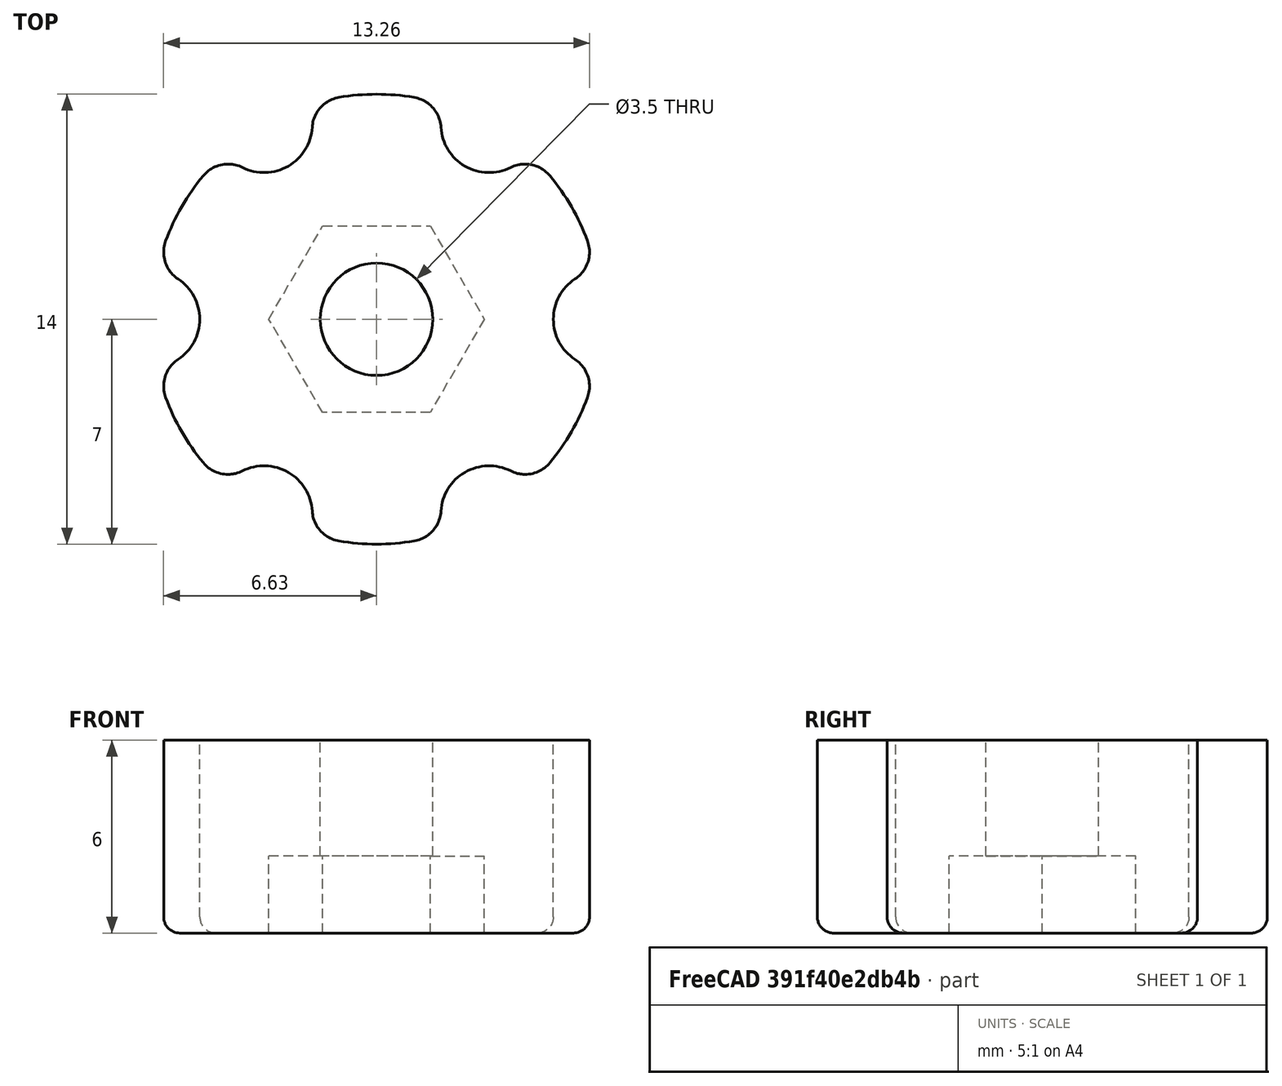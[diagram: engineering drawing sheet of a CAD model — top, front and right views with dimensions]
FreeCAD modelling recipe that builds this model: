
FCSTD DOCUMENT  (FreeCAD 0.19R24267 +99 (Git))
Label: ajustadorM3
License: All rights reserved
LicenseURL: http://en.wikipedia.org/wiki/All_rights_reserved
objects: Part::Cylinder×8, Part::Fillet×7, Part::MultiFuse×2, Part::Prism×1, Part::Cut×1, Part::Refine×1
note: 20 computed .brp shape members not serialized (recipe doc carries the construction recipe); baked Part::Feature solids carry a one-line shape summary decoded from their .brp

FEATURE [Part::Cylinder] cylinder
  Angle = 360
  AttacherType = Attacher::AttachEngine3D
  Height = 6
  Radius = 7
FEATURE [Part::Cylinder] cylinder001
  Angle = 360
  AttacherType = Attacher::AttachEngine3D
  Height = 100
  Placement = pos=(7,0,-50) rot=(0,0,1;0rad)
  Radius = 1.5
FEATURE [Part::Cylinder] cylinder002
  Angle = 360
  AttacherType = Attacher::AttachEngine3D
  Height = 100
  Placement = pos=(3.5,6.06218,-50) rot=(0,0,1;1.0472rad)
  Radius = 1.5
FEATURE [Part::Cylinder] cylinder003
  Angle = 360
  AttacherType = Attacher::AttachEngine3D
  Height = 100
  Placement = pos=(-3.5,6.06218,-50) rot=(0,0,1;2.0944rad)
  Radius = 1.5
FEATURE [Part::Cylinder] cylinder004
  Angle = 360
  AttacherType = Attacher::AttachEngine3D
  Height = 100
  Placement = pos=(-7,9e-16,-50) rot=(0,0,1;3.14159rad)
  Radius = 1.5
FEATURE [Part::Cylinder] cylinder005
  Angle = 360
  AttacherType = Attacher::AttachEngine3D
  Height = 100
  Placement = pos=(-3.5,-6.06218,-50) rot=(0,0,1;4.18879rad)
  Radius = 1.5
FEATURE [Part::Cylinder] cylinder006
  Angle = 360
  AttacherType = Attacher::AttachEngine3D
  Height = 100
  Placement = pos=(3.5,-6.06218,-50) rot=(0,0,-1;1.0472rad)
  Radius = 1.5
FEATURE [Part::MultiFuse] Group
  Shapes = -> [cylinder001,cylinder002,cylinder003,cylinder004,cylinder005,cylinder006]
FEATURE [Part::Prism] prism
  AttacherType = Attacher::AttachEngine3D
  Circumradius = 3.35
  FirstAngle = 0
  Height = 4.8
  Placement = pos=(0,0,-2.4) rot=(0,0,1;0rad)
  Polygon = 6
  SecondAngle = 0
FEATURE [Part::Cylinder] cylinder007
  Angle = 360
  AttacherType = Attacher::AttachEngine3D
  Height = 20
  Placement = pos=(0,0,-10) rot=(0,0,1;0rad)
  Radius = 1.75
FEATURE [Part::MultiFuse] union
  Shapes = -> [Group,prism,cylinder007]
FEATURE [Part::Cut] difference
  Base = -> cylinder
  Tool = -> union
FEATURE [Part::Refine] difference001
  Source = -> difference
FEATURE [Part::Fillet] Fillet
  Base = -> difference001
  Edges = 1 edges r=1: [Edge25]
FEATURE [Part::Fillet] Fillet001
  Base = -> Fillet
  Edges = 1 edges r=1: [Edge28]
FEATURE [Part::Fillet] Fillet002
  Base = -> Fillet001
  Edges = 1 edges r=1: [Edge29]
FEATURE [Part::Fillet] Fillet003
  Base = -> Fillet002
  Edges = 1 edges r=1: [Edge30]
FEATURE [Part::Fillet] Fillet004
  Base = -> Fillet003
  Edges = 1 edges r=1: [Edge31]
FEATURE [Part::Fillet] Fillet005
  Base = -> Fillet004
  Edges = 7 edges r=1: [Edge32,Edge36,Edge40,Edge44,Edge48,Edge52,Edge55]
FEATURE [Part::Fillet] Fillet006
  Base = -> Fillet005
  Edges = 1 edges r=0.5: [Edge9]
